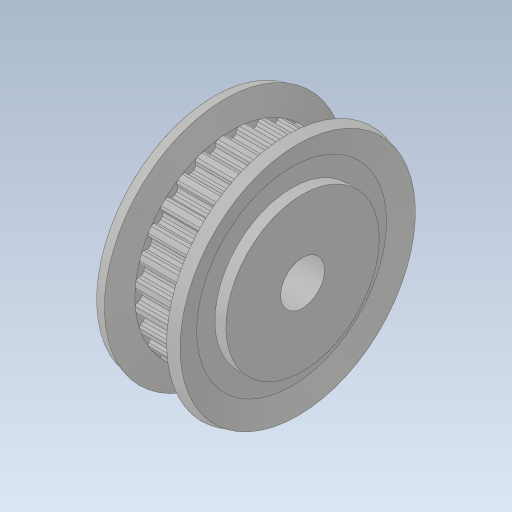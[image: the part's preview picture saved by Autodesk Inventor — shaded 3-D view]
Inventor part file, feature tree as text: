
AUTODESK INVENTOR PART (.ipt)
format: ipt  version: 2024 (Build 280153000, 153)  size: 402,944 bytes
history: native  units: mm
features: revolve x1, hole x1, extrude x1, pattern_circular x1, sketch x1
ambient origin geometry x8: Origin, YZ Plane, XZ Plane, XY Plane, X Axis, Y Axis, Z Axis, Center Point
bodies: Solid1 (feature_tree)
feature tree (5):
  revolve  "Revolution1"  [1 undecoded]
  hole  "Hole1"  [1 undecoded]
  extrude  "Extrusion1"  [1 undecoded]
  pattern_circular  "Circular Pattern1"  [2 undecoded]
  sketch  "Sketch2"  dims[d0=360.0deg d1=4.0mm d2=6.0mm d3=4.0mm d4=2.0mm d5=90.0deg d6=8.5mm d7=0.0mm d8=4.5mm d9=0.0mm d10=280.0mm d11=2.243995mm]
note: 5 required parameter values undecoded (feature->parameter linkage not recoverable at this tier; creation-order binding heuristic only, values carry confidence <= 0.55)